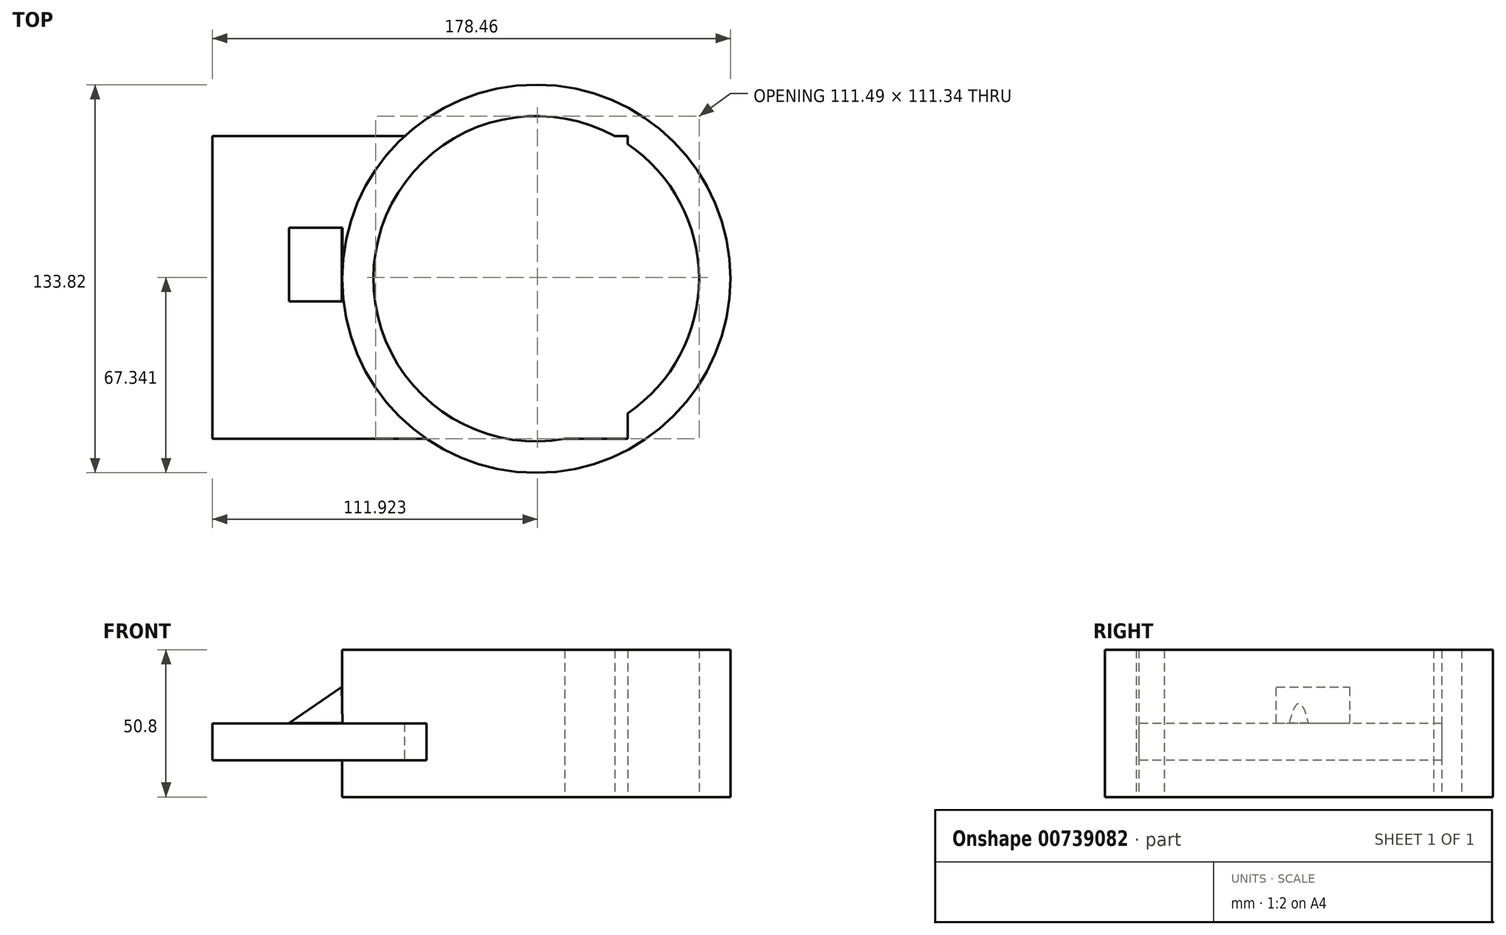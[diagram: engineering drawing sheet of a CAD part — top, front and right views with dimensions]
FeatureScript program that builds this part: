
annotation { "Feature Type Name" : "Feature", "Feature Type Description" : "" }
export const myFeature = defineFeature(function(context is Context, id is Id, definition is map)
    precondition{}
    {
        {
            var Q0;
            Q0=qCreatedBy(makeId("Top.planeOp"),FACE);
            var sketch = newSketch(context, id + "F0", { "sketchPlane" : qUnion([Q0])});
            skLineSegment(sketch, "E0.bottom", {"start": v(-69.15, 31.55) * mm, "end": v(73.96, 31.55) * mm});
            skLineSegment(sketch, "E0.top", {"start": v(-69.15, -72.86) * mm, "end": v(73.96, -72.86) * mm});
            skLineSegment(sketch, "E0.left", {"start": v(-69.15, 31.55) * mm, "end": v(-69.15, -72.86) * mm});
            skLineSegment(sketch, "E0.right", {"start": v(73.96, 31.55) * mm, "end": v(73.96, -72.86) * mm});
            skSolve(sketch);
        }
        {
            var Q0;
            Q0 = qSketchRegion(id + "F0", true);
            var Q1;
            Q1=makeQuery(id+"F0.imprint","IMPRINT",FACE,{"disambiguationData":[TD([[makeQuery(id+"F0.imprint","IMPRINT",EDGE,{"derivedFrom":sQuery(id+"F0.wireOp",EDGE,"E0.bottom")}),-1.0]])]});
            extrude(context, id + "F1", {"entities" : qUnion([Q0, Q1]), "depth" : 12.7 * mm, "offsetDistance" : 25.4 * mm});
        }
        {
            var Q0;
            Q0=makeQuery(id+"F1.opExtrude","CAP_FACE",FACE,{"disambiguationData":[OSD([sQuery(id+"F0.wireOp",EDGE,"E0.bottom"),sQuery(id+"F0.wireOp",EDGE,"E0.top"),sQuery(id+"F0.wireOp",EDGE,"E0.left"),sQuery(id+"F0.wireOp",EDGE,"E0.right")])],"isStart":false});
            var sketch = newSketch(context, id + "F2", { "sketchPlane" : qUnion([Q0])});
            skCircle(sketch, "E1", {"center": v(42.4, -17.62) * mm, "radius": 66.9 * mm});
            skCircle(sketch, "E2", {"center": v(42.4, -17.62) * mm, "radius": 56.12 * mm});
            skSolve(sketch);
        }
        {
            var Q0;
            {var subQ0=sQuery(id+"F2.wireOp",EDGE,"E1");var subQ1=makeQuery(id+"F1.opExtrude","CAP_EDGE",EDGE,{"disambiguationData":[OSD([sQuery(id+"F0.wireOp",EDGE,"E0.bottom")])],"isStart":false});var subQ2=makeQuery(id+"F2.imprint","INTERSECT",VERTEX,{"derivedFrom":[subQ1,subQ0]});Q0=makeQuery(id+"F2.imprint","IMPRINT",FACE,{"disambiguationData":[TD([[makeQuery(id+"F2.imprint","IMPRINT",EDGE,{"disambiguationData":[TD([[subQ2,-1.0]])],"derivedFrom":subQ0}),1.0]])]});}
            var Q1;
            {var subQ7=makeQuery(id+"F1.opExtrude","CAP_EDGE",EDGE,{"disambiguationData":[OSD([sQuery(id+"F0.wireOp",EDGE,"E0.bottom")])],"isStart":false});var subQ11=sQuery(id+"F2.wireOp",EDGE,"E1");var subQ12=makeQuery(id+"F2.imprint","INTERSECT",VERTEX,{"derivedFrom":[subQ7,subQ11]});Q1=makeQuery(id+"F2.imprint","IMPRINT",FACE,{"disambiguationData":[TD([[makeQuery(id+"F2.imprint","IMPRINT",EDGE,{"disambiguationData":[TD([[subQ12,1.0]])],"derivedFrom":subQ11}),1.0]])]});}
            extrude(context, id + "F3", {"entities" : qUnion([Q0, Q1]), "operationType" : NewBodyOperationType.ADD, "depth" : 25.4 * mm, "offsetDistance" : 25.4 * mm, "hasSecondDirection" : true, "secondDirectionOppositeDirection" : true, "secondDirectionDepth" : 25.4 * mm});
        }
        {
            var Q0;
            {var subQ1=sQuery(id+"F0.wireOp",EDGE,"E0.top");var subQ4=sQuery(id+"F0.wireOp",EDGE,"E0.bottom");var subQ7=sQuery(id+"F0.wireOp",EDGE,"E0.right");Q0=makeQuery(id+"F3.boolean.opBoolean","SPLIT",FACE,{"disambiguationData":[TD([makeQuery(id+"F1.opExtrude","SWEPT_FACE",FACE,{"disambiguationData":[OSD([subQ7])]})])],"derivedFrom":makeQuery(id+"F1.opExtrude","CAP_FACE",FACE,{"disambiguationData":[OSD([subQ4,subQ1,sQuery(id+"F0.wireOp",EDGE,"E0.left"),subQ7])],"isStart":false})});}
            extrude(context, id + "F4", {"entities" : qUnion([Q0]), "operationType" : NewBodyOperationType.REMOVE, "oppositeDirection" : true, "depth" : 25.4 * mm, "offsetDistance" : 25.4 * mm});
        }
        {
            var Q0;
            Q0=qCreatedBy(makeId("Front.planeOp"),FACE);
            var sketch = newSketch(context, id + "F5", { "sketchPlane" : qUnion([Q0])});
            skLineSegment(sketch, "E3", {"start": v(-24.57, 25.23) * mm, "end": v(-43.1, 12.62) * mm});
            skLineSegment(sketch, "E4", {"start": v(-43.1, 12.81) * mm, "end": v(-24.43, 12.81) * mm});
            skLineSegment(sketch, "E5", {"start": v(-24.43, 12.81) * mm, "end": v(-24.57, 25.23) * mm});
            skSolve(sketch);
        }
        {
            var Q0;
            {var subQ0=sQuery(id+"F5.wireOp",EDGE,"E5");Q0=makeQuery(id+"F5.imprint","IMPRINT",FACE,{"disambiguationData":[TD([[makeQuery(id+"F5.imprint","IMPRINT",EDGE,{"derivedFrom":subQ0}),1.0]])]});}
            extrude(context, id + "F6", {"entities" : qUnion([Q0]), "operationType" : NewBodyOperationType.ADD, "depth" : 25.4 * mm, "offsetDistance" : 25.4 * mm});
        }
    });
